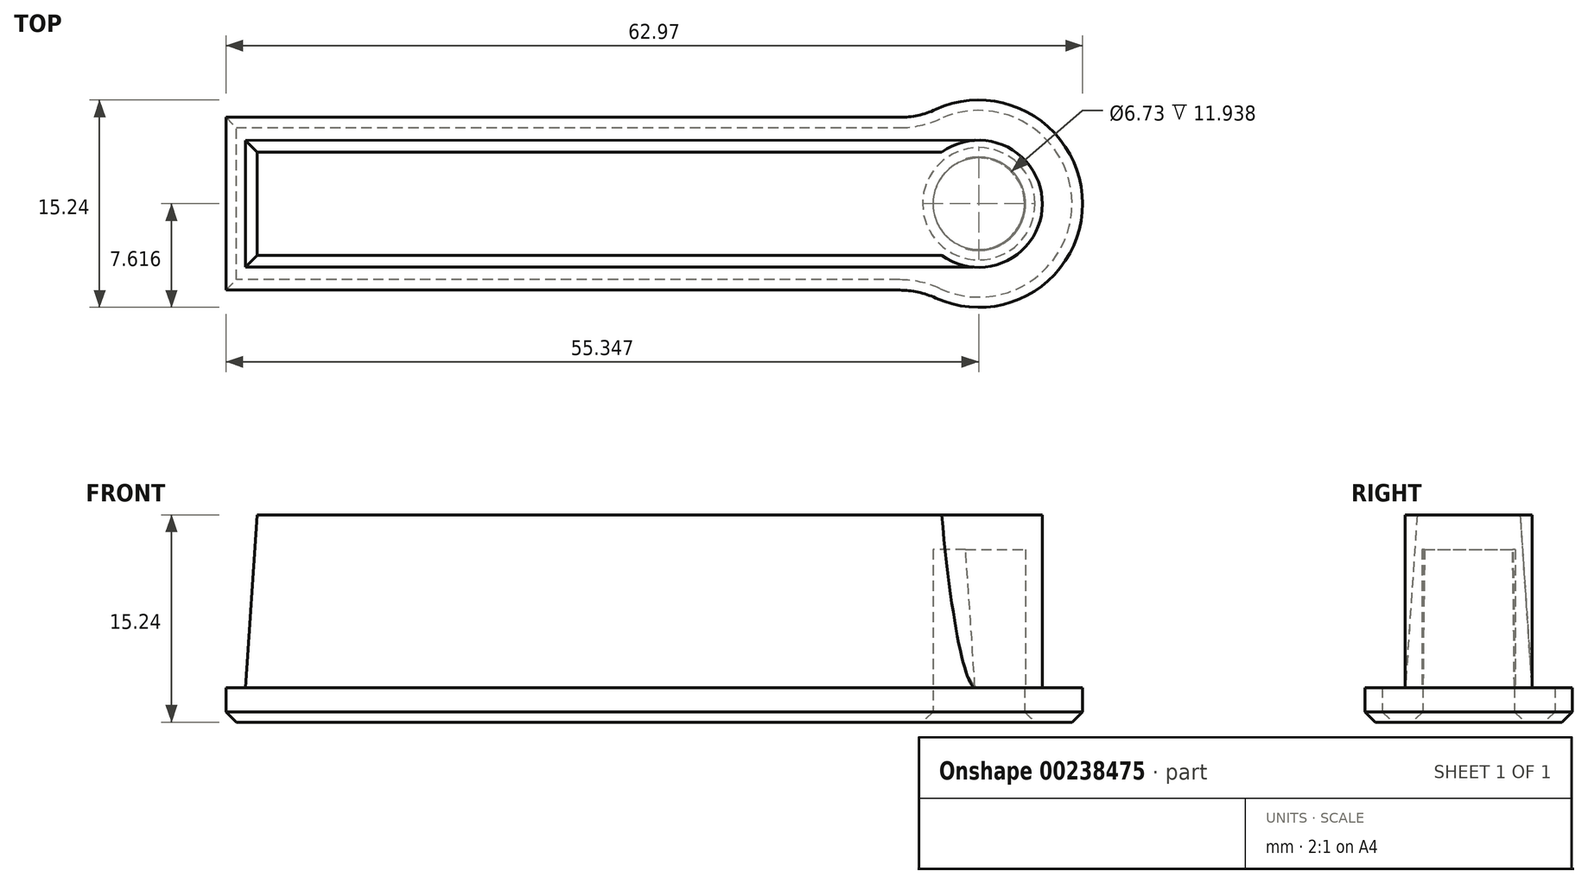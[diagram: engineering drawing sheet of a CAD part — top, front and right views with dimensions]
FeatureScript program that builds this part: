
annotation { "Feature Type Name" : "Feature", "Feature Type Description" : "" }
export const myFeature = defineFeature(function(context is Context, id is Id, definition is map)
    precondition{}
    {
        {
            var Q0;
            Q0=qCreatedBy(makeId("Top.planeOp"),FACE);
            var sketch = newSketch(context, id + "F0", { "sketchPlane" : qUnion([Q0])});
            skLineSegment(sketch, "E0", {"start": v(-50.8, 0) * mm, "end": v(-50.8, 9.65) * mm});
            skLineSegment(sketch, "E1", {"start": v(-50.8, 9.65) * mm, "end": v(3.18, 9.67) * mm});
            skLineSegment(sketch, "E2", {"start": v(3.17, 9.67) * mm, "end": v(3.18, 0) * mm});
            skLineSegment(sketch, "E3", {"start": v(3.18, 0) * mm, "end": v(-50.8, 0) * mm});
            skPoint(sketch, "E4.orphan", {"position": v(10.16, 0) * mm});
            skPoint(sketch, "E5.orphan", {"position": v(3.18, 7.62) * mm});
            skPoint(sketch, "E6.orphan", {"position": v(0, 9.67) * mm});
            skSolve(sketch);
        }
        {
            var Q0;
            Q0 = qSketchRegion(id + "F0", true);
            extrude(context, id + "F1", {"entities" : qUnion([Q0]), "depth" : 15.24 * mm, "hasDraft" : true, "draftAngle" : 3.9 * degree, "draftPullDirection" : true});
        }
        {
            var Q0;
            Q0=makeQuery(id+"F1.opExtrude","CAP_FACE",FACE,{"disambiguationData":[OSD([sQuery(id+"F0.wireOp",EDGE,"E0"),sQuery(id+"F0.wireOp",EDGE,"E1"),sQuery(id+"F0.wireOp",EDGE,"57ZeFkwo-vLvJ-xJX7-h7Uu-BIM3K8O7cLfX"),sQuery(id+"F0.wireOp",EDGE,"YFwLEkJ7-Ctef-bccI-dQv7-4AmSqifM5cD3"),sQuery(id+"F0.wireOp",EDGE,"E2"),sQuery(id+"F0.wireOp",EDGE,"NS4WsYP2-6mqE-ukSs-TuaD-KOdCxSYbY5gJ"),sQuery(id+"F0.wireOp",EDGE,"hDCIGdzC-Qy6f-o0JE-DSoz-13bcDaxCQowz"),sQuery(id+"F0.wireOp",EDGE,"E3")])],"isStart":true});
            var sketch = newSketch(context, id + "F2", { "sketchPlane" : qUnion([Q0])});
            skLineSegment(sketch, "E7", {"start": v(-49.76, -4.83) * mm, "end": v(17.09, -4.83) * mm, "construction": true});
            skPoint(sketch, "E7.endSnap0", {"position": v(-49.76, -4.83) * mm});
            skArc(sketch, "E8", {"start": v(0.1, -11.75) * mm, "mid": v(10.9, -4.83) * mm, "end": v(0.1, 2.1) * mm});
            skLineSegment(sketch, "E9", {"start": v(-2.54, 1.52) * mm, "end": v(-52.07, 1.52) * mm});
            skLineSegment(sketch, "E10", {"start": v(-52.07, 1.52) * mm, "end": v(-52.07, -11.18) * mm});
            skLineSegment(sketch, "E11", {"start": v(-52.07, -11.18) * mm, "end": v(-2.54, -11.18) * mm});
            skPoint(sketch, "E12.visualSharp", {"position": v(-0.94, 1.52) * mm});
            skArc(sketch, "E12.filletArc", {"start": v(-2.54, 1.52) * mm, "mid": v(-1.19, 1.67) * mm, "end": v(0.1, 2.1) * mm});
            skPoint(sketch, "E13.visualSharp", {"position": v(-0.94, -11.18) * mm});
            skArc(sketch, "E13.filletArc", {"start": v(0.1, -11.75) * mm, "mid": v(-1.19, -11.32) * mm, "end": v(-2.54, -11.18) * mm});
            skSolve(sketch);
        }
        {
            var Q0;
            Q0 = qSketchRegion(id + "F2", true);
            extrude(context, id + "F3", {"entities" : qUnion([Q0]), "operationType" : NewBodyOperationType.ADD, "oppositeDirection" : true, "depth" : 2.54 * mm});
        }
        {
            var Q0;
            Q0=makeQuery(id+"F3.boolean.opBoolean","MERGE",FACE,{"derivedFrom":[makeQuery(id+"F1.opExtrude","CAP_FACE",FACE,{"disambiguationData":[OSD([sQuery(id+"F0.wireOp",EDGE,"E0"),sQuery(id+"F0.wireOp",EDGE,"E1"),sQuery(id+"F0.wireOp",EDGE,"57ZeFkwo-vLvJ-xJX7-h7Uu-BIM3K8O7cLfX"),sQuery(id+"F0.wireOp",EDGE,"YFwLEkJ7-Ctef-bccI-dQv7-4AmSqifM5cD3"),sQuery(id+"F0.wireOp",EDGE,"E2"),sQuery(id+"F0.wireOp",EDGE,"NS4WsYP2-6mqE-ukSs-TuaD-KOdCxSYbY5gJ"),sQuery(id+"F0.wireOp",EDGE,"hDCIGdzC-Qy6f-o0JE-DSoz-13bcDaxCQowz"),sQuery(id+"F0.wireOp",EDGE,"E3")])],"isStart":true}),makeQuery(id+"F3.opExtrude","CAP_FACE",FACE,{"disambiguationData":[OSD([sQuery(id+"F2.wireOp",EDGE,"E8")])],"isStart":true})]});
            var sketch = newSketch(context, id + "F4", { "sketchPlane" : qUnion([Q0])});
            skCircle(sketch, "E14", {"center": v(3.28, -4.83) * mm, "radius": 3.37 * mm});
            skSolve(sketch);
        }
        {
            var Q0;
            Q0 = qSketchRegion(id + "F4", true);
            extrude(context, id + "F5", {"entities" : qUnion([Q0]), "operationType" : NewBodyOperationType.REMOVE, "oppositeDirection" : true, "depth" : 12.7 * mm});
        }
        {
            var Q0;
            {var subQ0=sQuery(id+"F2.wireOp",EDGE,"E8");Q0=makeQuery(id+"F3.boolean.opBoolean","SPLIT",FACE,{"disambiguationData":[TD([makeQuery(id+"F1.opExtrude","SWEPT_FACE",FACE,{"disambiguationData":[OSD([sQuery(id+"F0.wireOp",EDGE,"E1")])]})])],"derivedFrom":makeQuery(id+"F3.opExtrude","CAP_FACE",FACE,{"disambiguationData":[OSD([subQ0])],"isStart":false})});}
            var sketch = newSketch(context, id + "F6", { "sketchPlane" : qUnion([Q0])});
            skCircle(sketch, "E15", {"center": v(3.28, 4.83) * mm, "radius": 3.43 * mm});
            skCircle(sketch, "E16", {"center": v(3.28, 4.83) * mm, "radius": 4.67 * mm});
            skSolve(sketch);
        }
        {
            var Q0;
            Q0 = qSketchRegion(id + "F6", true);
            extrude(context, id + "F7", {"entities" : qUnion([Q0]), "operationType" : NewBodyOperationType.ADD, "depth" : 12.7 * mm});
        }
        {
            var Q0;
            Q0=makeQuery(id+"F7.boolean.opBoolean","MERGE",FACE,{"derivedFrom":[makeQuery(id+"F1.opExtrude","CAP_FACE",FACE,{"disambiguationData":[OSD([sQuery(id+"F0.wireOp",EDGE,"E0"),sQuery(id+"F0.wireOp",EDGE,"E1"),sQuery(id+"F0.wireOp",EDGE,"57ZeFkwo-vLvJ-xJX7-h7Uu-BIM3K8O7cLfX"),sQuery(id+"F0.wireOp",EDGE,"YFwLEkJ7-Ctef-bccI-dQv7-4AmSqifM5cD3"),sQuery(id+"F0.wireOp",EDGE,"E2"),sQuery(id+"F0.wireOp",EDGE,"NS4WsYP2-6mqE-ukSs-TuaD-KOdCxSYbY5gJ"),sQuery(id+"F0.wireOp",EDGE,"hDCIGdzC-Qy6f-o0JE-DSoz-13bcDaxCQowz"),sQuery(id+"F0.wireOp",EDGE,"E3")])],"isStart":false}),makeQuery(id+"F7.opExtrude","CAP_FACE",FACE,{"disambiguationData":[OSD([sQuery(id+"F6.wireOp",EDGE,"E15"),sQuery(id+"F6.wireOp",EDGE,"E16")])],"isStart":false})]});
            var sketch = newSketch(context, id + "F8", { "sketchPlane" : qUnion([Q0])});
            skCircle(sketch, "E17", {"center": v(3.28, 4.83) * mm, "radius": 3.8 * mm});
            skSolve(sketch);
        }
        {
            var Q0;
            Q0 = qSketchRegion(id + "F8", true);
            extrude(context, id + "F9", {"entities" : qUnion([Q0]), "operationType" : NewBodyOperationType.ADD, "oppositeDirection" : true, "depth" : 2.54 * mm});
        }
        {
            var Q0;
            Q0=makeQuery(id+"F3.boolean.opBoolean","MERGE",FACE,{"derivedFrom":[makeQuery(id+"F1.opExtrude","CAP_FACE",FACE,{"disambiguationData":[OSD([sQuery(id+"F0.wireOp",EDGE,"E0"),sQuery(id+"F0.wireOp",EDGE,"E1"),sQuery(id+"F0.wireOp",EDGE,"E2"),sQuery(id+"F0.wireOp",EDGE,"E3")])],"isStart":true}),makeQuery(id+"F3.opExtrude","CAP_FACE",FACE,{"disambiguationData":[OSD([sQuery(id+"F2.wireOp",EDGE,"E8"),sQuery(id+"F2.wireOp",EDGE,"E9"),sQuery(id+"F2.wireOp",EDGE,"E10"),sQuery(id+"F2.wireOp",EDGE,"E11"),sQuery(id+"F2.wireOp",EDGE,"E12.filletArc"),sQuery(id+"F2.wireOp",EDGE,"E13.filletArc")])],"isStart":true})]});
            chamfer(context, id + "F10", {"entities" : qUnion([Q0]), "width" : 0.76 * mm, "tangentPropagation" : true});
        }
    });
